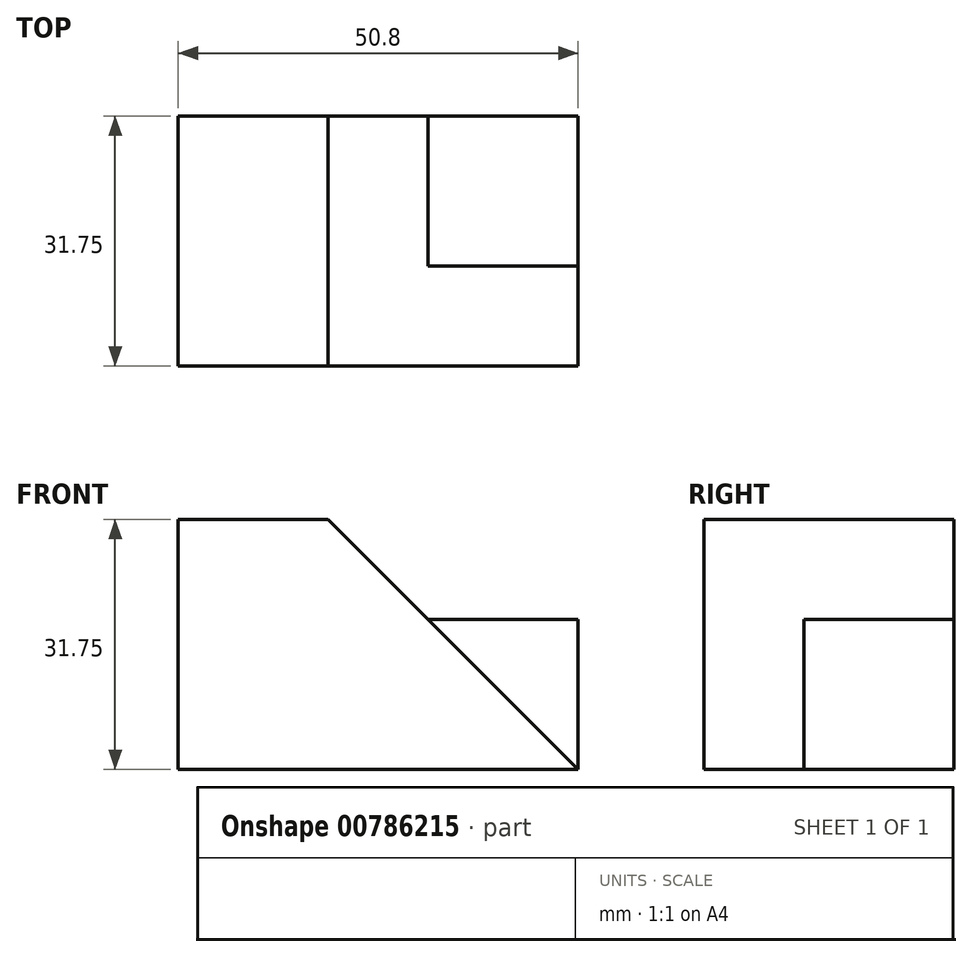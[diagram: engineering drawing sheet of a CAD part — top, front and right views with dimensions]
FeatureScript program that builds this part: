
annotation { "Feature Type Name" : "Feature", "Feature Type Description" : "" }
export const myFeature = defineFeature(function(context is Context, id is Id, definition is map)
    precondition{}
    {
        {
            var Q0;
            Q0=qCreatedBy(makeId("Front.planeOp"),FACE);
            var sketch = newSketch(context, id + "F0", { "sketchPlane" : qUnion([Q0])});
            skLineSegment(sketch, "E0", {"start": v(0, 0) * mm, "end": v(50.8, 0) * mm});
            skLineSegment(sketch, "E1", {"start": v(50.8, 0) * mm, "end": v(50.8, 31.75) * mm});
            skLineSegment(sketch, "E2", {"start": v(50.8, 31.75) * mm, "end": v(0, 31.75) * mm});
            skLineSegment(sketch, "E3", {"start": v(0, 31.75) * mm, "end": v(0, 0) * mm});
            skSolve(sketch);
        }
        {
            var Q0;
            Q0 = qSketchRegion(id + "F0", true);
            extrude(context, id + "F1", {"entities" : qUnion([Q0]), "depth" : 31.75 * mm, "offsetDistance" : 25.4 * mm});
        }
        {
            var Q0;
            Q0=makeQuery(id+"F1.opExtrude","CAP_FACE",FACE,{"disambiguationData":[OSD([sQuery(id+"F0.wireOp",EDGE,"E0"),sQuery(id+"F0.wireOp",EDGE,"E1"),sQuery(id+"F0.wireOp",EDGE,"E2"),sQuery(id+"F0.wireOp",EDGE,"E3")])],"isStart":false});
            var sketch = newSketch(context, id + "F2", { "sketchPlane" : qUnion([Q0])});
            skLineSegment(sketch, "E4", {"start": v(0, 31.75) * mm, "end": v(19.05, 31.75) * mm});
            skLineSegment(sketch, "E5", {"start": v(19.05, 31.75) * mm, "end": v(50.8, 0) * mm});
            skLineSegment(sketch, "E6", {"start": v(50.8, 0) * mm, "end": v(31.75, 0) * mm});
            skLineSegment(sketch, "E7", {"start": v(31.75, 0) * mm, "end": v(31.75, 19.05) * mm});
            skLineSegment(sketch, "E8", {"start": v(31.75, 19.05) * mm, "end": v(50.8, 19.05) * mm});
            skSolve(sketch);
        }
        {
            var Q0;
            {var subQ3=sQuery(id+"F2.wireOp",EDGE,"E8");Q0=makeQuery(id+"F2.imprint","IMPRINT",FACE,{"disambiguationData":[TD([[makeQuery(id+"F2.imprint","IMPRINT",EDGE,{"derivedFrom":subQ3}),1.0]])]});}
            extrude(context, id + "F3", {"entities" : qUnion([Q0]), "operationType" : NewBodyOperationType.REMOVE, "oppositeDirection" : true, "depth" : 38.1 * mm, "offsetDistance" : 25.4 * mm});
        }
        {
            var Q0;
            Q0=makeQuery(id+"F1.opExtrude","CAP_FACE",FACE,{"disambiguationData":[OSD([sQuery(id+"F0.wireOp",EDGE,"E0"),sQuery(id+"F0.wireOp",EDGE,"E1"),sQuery(id+"F0.wireOp",EDGE,"E2"),sQuery(id+"F0.wireOp",EDGE,"E3")])],"isStart":false});
            var sketch = newSketch(context, id + "F4", { "sketchPlane" : qUnion([Q0])});
            skLineSegment(sketch, "E9", {"start": v(31.75, 19.05) * mm, "end": v(50.8, 0) * mm});
            skSolve(sketch);
        }
        {
            var Q0;
            Q0=makeQuery(id+"F4.imprint","IMPRINT",FACE,{"disambiguationData":[TD([[makeQuery(id+"F4.imprint","IMPRINT",EDGE,{"derivedFrom":sQuery(id+"F4.wireOp",EDGE,"E9")}),1.0]])]});
            extrude(context, id + "F5", {"entities" : qUnion([Q0]), "operationType" : NewBodyOperationType.REMOVE, "oppositeDirection" : true, "depth" : 12.7 * mm, "offsetDistance" : 25.4 * mm});
        }
    });
